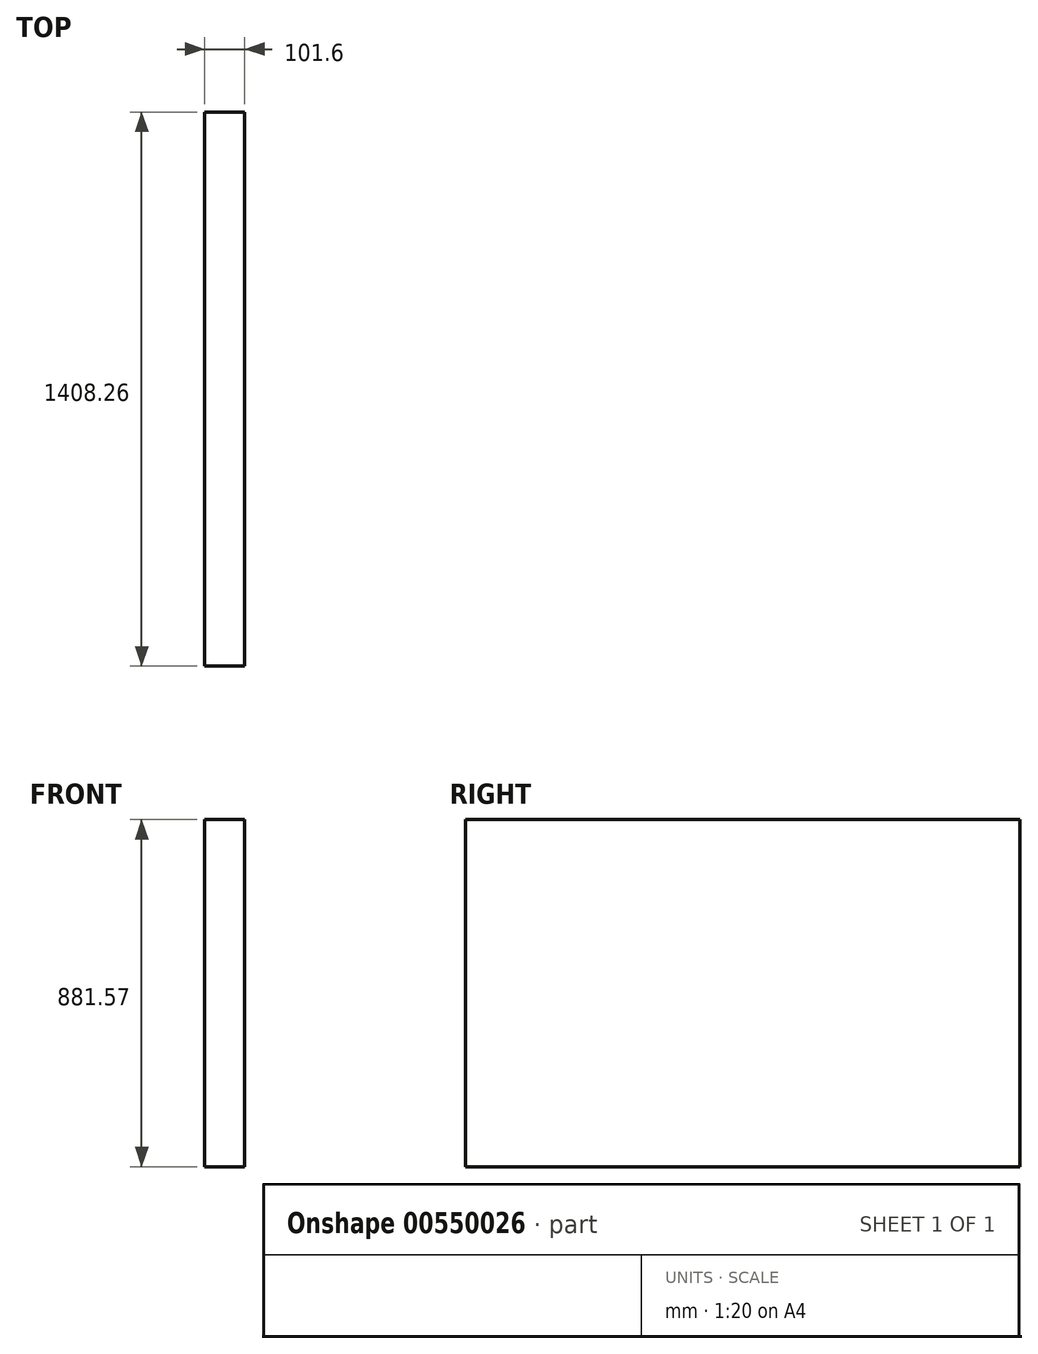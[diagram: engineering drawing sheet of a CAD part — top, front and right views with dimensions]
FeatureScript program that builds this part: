
annotation { "Feature Type Name" : "Feature", "Feature Type Description" : "" }
export const myFeature = defineFeature(function(context is Context, id is Id, definition is map)
    precondition{}
    {
        {
            var Q0;
            Q0=qCreatedBy(makeId("Right.planeOp"),FACE);
            var sketch = newSketch(context, id + "F0", { "sketchPlane" : qUnion([Q0])});
            skLineSegment(sketch, "E0.bottom", {"start": v(-672.02, 379.7) * mm, "end": v(736.24, 379.7) * mm});
            skLineSegment(sketch, "E0.top", {"start": v(-672.02, -501.86) * mm, "end": v(736.24, -501.86) * mm});
            skLineSegment(sketch, "E0.left", {"start": v(-672.02, 379.7) * mm, "end": v(-672.02, -501.86) * mm});
            skLineSegment(sketch, "E0.right", {"start": v(736.24, 379.7) * mm, "end": v(736.24, -501.86) * mm});
            skSolve(sketch);
        }
        {
            var Q0;
            Q0=makeQuery(id+"F0.imprint","IMPRINT",FACE,{"disambiguationData":[TD([[makeQuery(id+"F0.imprint","IMPRINT",EDGE,{"derivedFrom":sQuery(id+"F0.wireOp",EDGE,"E0.bottom")}),-1.0]])]});
            extrude(context, id + "F1", {"entities" : qUnion([Q0]), "depth" : 25.4 * mm, "offsetDistance" : 25.4 * mm, "hasSecondDirection" : true, "secondDirectionOppositeDirection" : true, "secondDirectionDepth" : 76.2 * mm});
        }
    });
